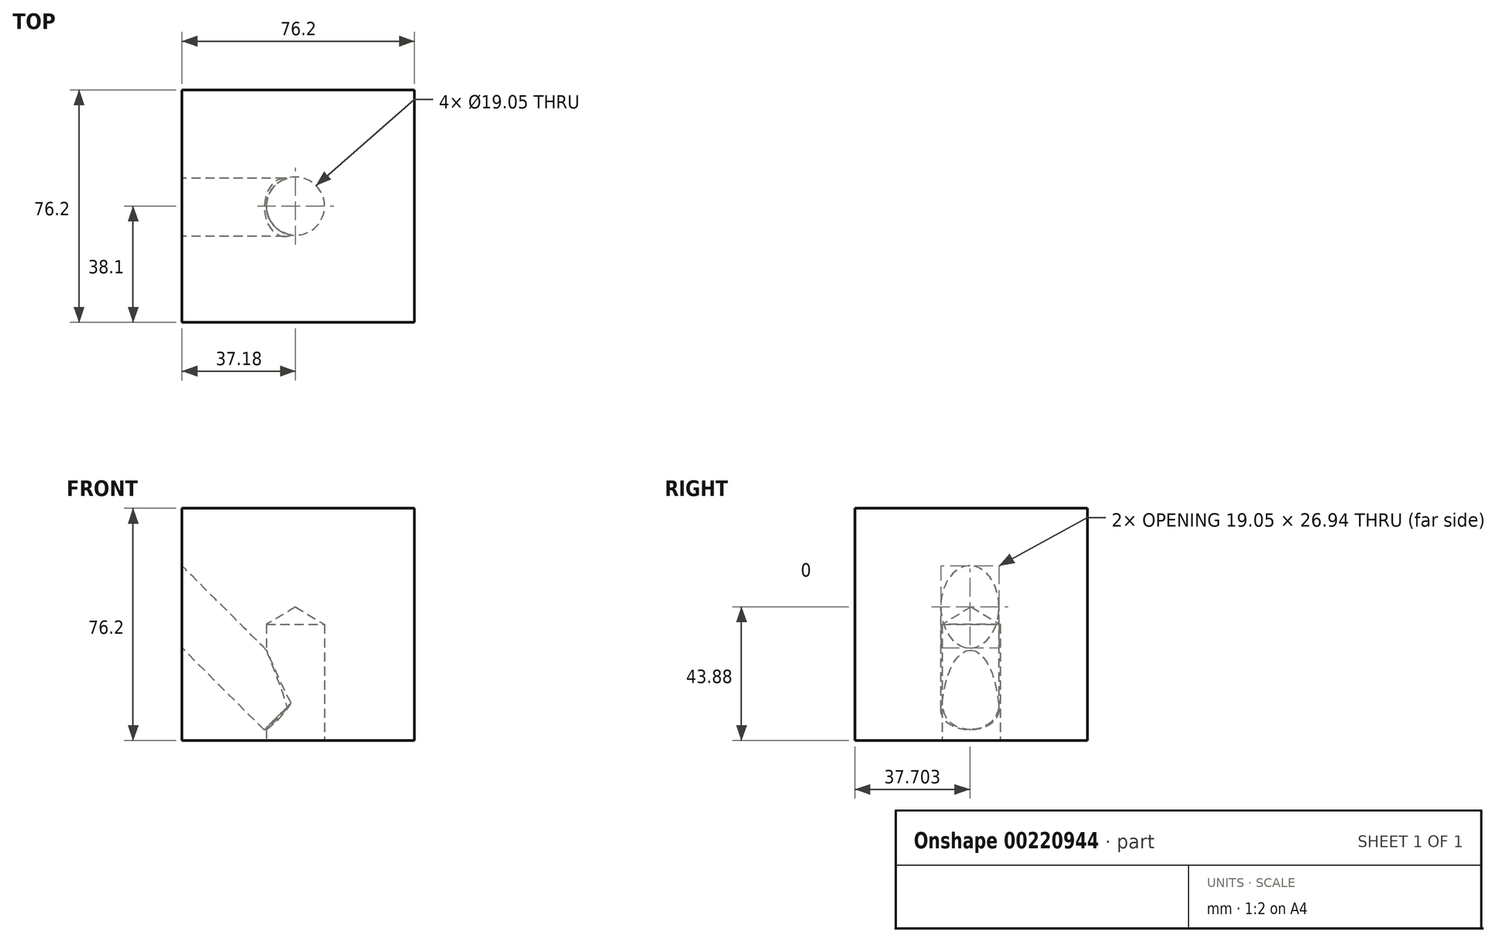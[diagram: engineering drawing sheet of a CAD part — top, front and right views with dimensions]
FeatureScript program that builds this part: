
annotation { "Feature Type Name" : "Feature", "Feature Type Description" : "" }
export const myFeature = defineFeature(function(context is Context, id is Id, definition is map)
    precondition{}
    {
        {
            var Q0;
            Q0=qCreatedBy(makeId("Front.planeOp"),FACE);
            var sketch = newSketch(context, id + "F0", { "sketchPlane" : qUnion([Q0])});
            skLineSegment(sketch, "E0.bottom", {"start": v(-37.18, 32.41) * mm, "end": v(39.02, 32.41) * mm});
            skLineSegment(sketch, "E0.top", {"start": v(-37.18, -43.79) * mm, "end": v(39.02, -43.79) * mm});
            skLineSegment(sketch, "E0.left", {"start": v(-37.18, 32.41) * mm, "end": v(-37.18, -43.79) * mm});
            skLineSegment(sketch, "E0.right", {"start": v(39.02, 32.41) * mm, "end": v(39.02, -43.79) * mm});
            skSolve(sketch);
        }
        {
            var Q0;
            Q0=makeQuery(id+"F0.imprint","IMPRINT",FACE,{"disambiguationData":[TD([[makeQuery(id+"F0.imprint","IMPRINT",EDGE,{"derivedFrom":sQuery(id+"F0.wireOp",EDGE,"E0.bottom")}),-1.0]])]});
            extrude(context, id + "F1", {"entities" : qUnion([Q0]), "depth" : 76.2 * mm});
        }
        {
            var Q0;
            Q0=makeQuery(id+"F1.opExtrude","SWEPT_FACE",FACE,{"disambiguationData":[OSD([sQuery(id+"F0.wireOp",EDGE,"E0.top")])]});
            var sketch = newSketch(context, id + "F2", { "sketchPlane" : qUnion([Q0])});
            skCircle(sketch, "E1", {"center": v(0, 38.1) * mm, "radius": 9.53 * mm});
            skSolve(sketch);
        }
        {
            var Q0;
            Q0=sQuery(id+"F2.wireOp",VERTEX,"E1.center");
            var Q1;
            Q1=makeQuery(id+"F1.opExtrude","SWEPT_BODY",BODY,{"disambiguationData":[OSD([sQuery(id+"F0.wireOp",EDGE,"E0.bottom"),sQuery(id+"F0.wireOp",EDGE,"E0.top"),sQuery(id+"F0.wireOp",EDGE,"E0.left"),sQuery(id+"F0.wireOp",EDGE,"E0.right")])]});
            hole(context, id + "F3", {"style" : HoleStyle.SIMPLE, "endStyle" : HoleEndStyle.BLIND, "holeDiameter" : 19.05 * mm, "holeDepth" : 38.1 * mm, "locations" : qUnion([Q0]), "scope" : qUnion([Q1])});
        }
        {
            var Q0;
            Q0=makeQuery(id+"F1.opExtrude","SWEPT_EDGE",EDGE,{"disambiguationData":[OSD([sQuery(id+"F0.wireOp",EDGE,"E0.bottom"),sQuery(id+"F0.wireOp",EDGE,"E0.left")])]});
            var Q1;
            Q1=makeQuery(id+"F1.opExtrude","SWEPT_EDGE",EDGE,{"disambiguationData":[OSD([sQuery(id+"F0.wireOp",EDGE,"E0.top"),sQuery(id+"F0.wireOp",EDGE,"E0.left")])]});
            cPlane(context, id + "F4", {"entities" : qUnion([Q0, Q1]), "cplaneType" : CPlaneType.LINE_ANGLE, "offset" : 25.4 * mm, "angle" : 45 * degree, "width" : 152.4 * mm, "height" : 152.4 * mm});
        }
        {
            var Q0;
            Q0=qCreatedBy(id+"F4.planeOp",FACE);
            var sketch = newSketch(context, id + "F5", { "sketchPlane" : qUnion([Q0])});
            skCircle(sketch, "E2", {"center": v(38.5, -26.22) * mm, "radius": 9.53 * mm});
            skSolve(sketch);
        }
        {
            var Q0;
            Q0=sQuery(id+"F5.wireOp",VERTEX,"E2.center");
            var Q1;
            Q1=makeQuery(id+"F1.opExtrude","SWEPT_BODY",BODY,{"disambiguationData":[OSD([sQuery(id+"F0.wireOp",EDGE,"E0.bottom"),sQuery(id+"F0.wireOp",EDGE,"E0.top"),sQuery(id+"F0.wireOp",EDGE,"E0.left"),sQuery(id+"F0.wireOp",EDGE,"E0.right")])]});
            hole(context, id + "F6", {"style" : HoleStyle.SIMPLE, "endStyle" : HoleEndStyle.BLIND, "holeDiameter" : 19.05 * mm, "holeDepth" : 38.1 * mm, "locations" : qUnion([Q0]), "scope" : qUnion([Q1])});
        }
    });
